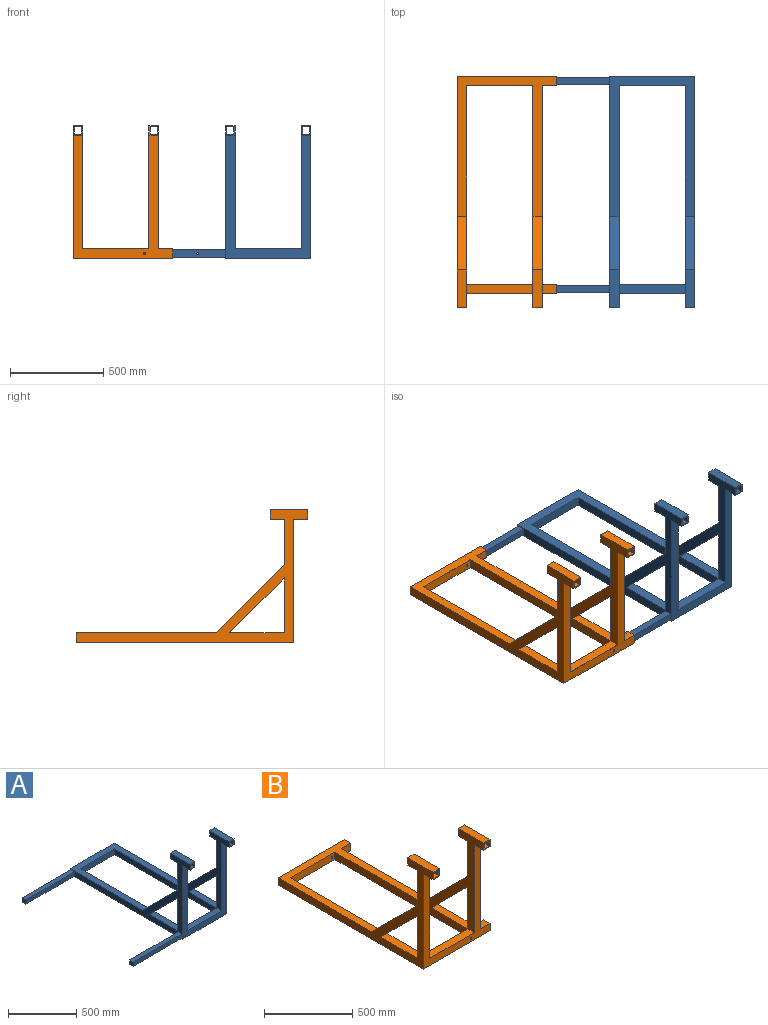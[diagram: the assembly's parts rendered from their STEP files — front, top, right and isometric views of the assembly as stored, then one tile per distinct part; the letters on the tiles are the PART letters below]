
ASSEMBLY  parts=2 mates=1
PART A: 53 faces, bbox 965.2x1244.6x711.2 mm
  f0: plane 50.8x50.8mm, normal (0,1,0), area 1129mm2, adj f9,f12,f13,f24,f35,f36,f37,f38
  f1: plane 50.8x50.8mm, normal (0,-1,0), area 1129mm2, adj f9,f12,f13,f30,f35,f36,f37,f38
  f2: plane 50.8x50.8mm, normal (0,1,0), area 1129mm2, adj f11,f15,f16,f17,f31,f32,f33,f34
  f3: plane 50.8x50.8mm, normal (0,-1,0), area 1129mm2, adj f11,f15,f16,f29,f31,f32,f33,f34
  f4: plane 660.4x457.2mm, normal (0,-1,0), area 85161.1mm2, adj f5,f9,f11,f13,f14,f15,f29,f30
  f5: plane 1168.4x457.2mm, normal (0,0,-1), area 154838.4mm2, adj f4,f9,f10,f11,f13,f15,f27,f28
  f6: plane 751.48x457.2mm, normal (0,0,1), area 94414.8mm2, adj f9,f10,f11,f13,f15,f19,f22,f27
  f7: plane 294.28x50.8mm, normal (0,0,1), area 14949.4mm2, adj f11,f15,f20,f21
  f8: plane 294.28x50.8mm, normal (0,0,1), area 14949.4mm2, adj f9,f13,f25,f26
  f9: plane 1244.6x711.2mm, normal (1,0,0), area 124367mm2, adj f0,f1,f4,f5,f6,f8,f10,f12
  f10: plane 457.2x50.8mm, normal (0,1,0), area 23225.8mm2, adj f5,f6,f9,f11
  f11: plane 1244.6x711.2mm, normal (-1,0,0), area 121463.8mm2, adj f2,f3,f4,f5,f6,f7,f10,f16
  f12: plane 203.2x50.8mm, normal (0,0,1), area 10322.6mm2, adj f0,f1,f9,f13
  f13: plane 1193.8x711.2mm, normal (-1,0,0), area 119205.7mm2, adj f0,f1,f4,f5,f6,f8,f12,f14
  f14: plane 355.6x50.8mm, normal (0,0,1), area 18064.5mm2, adj f4,f13,f15,f28
  f15: plane 1193.8x711.2mm, normal (1,0,0), area 119205.7mm2, adj f2,f3,f4,f5,f6,f7,f14,f16
  f16: plane 203.2x50.8mm, normal (0,0,1), area 10322.6mm2, adj f2,f3,f11,f15
  f17: plane 76.2x50.8mm, normal (0,0,-1), area 3871mm2, adj f2,f11,f15,f18
  f18: plane 243.48x50.8mm, normal (0,1,0), area 12368.7mm2, adj f11,f15,f17,f19
  f19: plane 366.12x366.12mm, normal (0,0.71,0.71), area 26302.9mm2, adj f6,f11,f15,f18
  f20: plane 294.28x294.28mm, normal (0,-0.71,-0.71), area 21141.6mm2, adj f7,f11,f15,f21
  f21: plane 294.28x50.8mm, normal (0,1,0), area 14949.4mm2, adj f7,f11,f15,f20
  f22: plane 366.12x366.12mm, normal (0,0.71,0.71), area 26302.9mm2, adj f6,f9,f13,f23
  f23: plane 243.48x50.8mm, normal (0,1,0), area 12368.7mm2, adj f9,f13,f22,f24
  f24: plane 76.2x50.8mm, normal (0,0,-1), area 3871mm2, adj f0,f9,f13,f23
  f25: plane 294.28x50.8mm, normal (0,1,0), area 14949.4mm2, adj f8,f9,f13,f26
  f26: plane 294.28x294.28mm, normal (0,-0.71,-0.71), area 21141.6mm2, adj f8,f9,f13,f25
  f27: plane 355.6x50.8mm, normal (0,-1,0), area 18064.5mm2, adj f5,f6,f13,f15
  f28: plane 355.6x50.8mm, normal (0,1,0), area 18064.5mm2, adj f5,f13,f14,f15
  f29: plane 76.2x50.8mm, normal (0,0,-1), area 3871mm2, adj f3,f4,f11,f15
  f30: plane 76.2x50.8mm, normal (0,0,-1), area 3871mm2, adj f1,f4,f9,f13
  f31: plane 203.2x38.1mm, normal (-1,0,0), area 7741.9mm2, adj f2,f3,f32,f34
  f32: plane 203.2x38.1mm, normal (0,0,-1), area 7741.9mm2, adj f2,f3,f31,f33
  f33: plane 203.2x38.1mm, normal (1,0,0), area 7741.9mm2, adj f2,f3,f32,f34
  f34: plane 203.2x38.1mm, normal (0,0,1), area 7741.9mm2, adj f2,f3,f31,f33
  f35: plane 203.2x38.1mm, normal (-1,0,0), area 7741.9mm2, adj f0,f1,f36,f38
  f36: plane 203.2x38.1mm, normal (0,0,-1), area 7741.9mm2, adj f0,f1,f35,f37
  f37: plane 203.2x38.1mm, normal (1,0,0), area 7741.9mm2, adj f0,f1,f36,f38
  f38: plane 203.2x38.1mm, normal (0,0,1), area 7741.9mm2, adj f0,f1,f35,f37
  f39: plane 508x38.1mm, normal (0,-1,0), area 19101.4mm2, adj f11,f40,f42,f43,f51,f52
  f40: plane 508x38.1mm, normal (0,0,1), area 19354.8mm2, adj f11,f39,f41,f43
  f41: plane 508x38.1mm, normal (0,1,0), area 19101.4mm2, adj f11,f40,f42,f43,f51,f52
  f42: plane 508x38.1mm, normal (0,0,-1), area 19354.8mm2, adj f11,f39,f41,f43
  f43: plane 38.1x38.1mm, normal (-1,0,0), area 1451.6mm2, adj f39,f40,f41,f42
  f44: plane 508x38.1mm, normal (0,0,1), area 19354.8mm2, adj f11,f45,f47,f48
  f45: plane 508x38.1mm, normal (0,1,0), area 19101.4mm2, adj f11,f44,f46,f48,f49,f50
  f46: plane 508x38.1mm, normal (0,0,-1), area 19354.8mm2, adj f11,f45,f47,f48
  f47: plane 508x38.1mm, normal (0,-1,0), area 19101.4mm2, adj f11,f44,f46,f48,f49,f50
  f48: plane 38.1x38.1mm, normal (-1,0,0), area 1451.6mm2, adj f44,f45,f46,f47
  f49: cylinder r=6.35mm len=38.1mm, axis (0,-1,0), area 1520.1mm2, adj f45,f47
  f50: cylinder r=6.35mm len=38.1mm, axis (0,-1,0), area 1520.1mm2, adj f45,f47
  f51: cylinder r=6.35mm len=38.1mm, axis (0,-1,0), area 1520.1mm2, adj f39,f41
  f52: cylinder r=6.35mm len=38.1mm, axis (0,-1,0), area 1520.1mm2, adj f39,f41
PART B: 74 faces, bbox 533.4x1244.6x711.2 mm
  f0: plane 50.8x50.8mm, normal (1,0,0), area 1129mm2, adj f7,f10,f12,f31,f47,f50,f52,f67
  f1: plane 50.8x50.8mm, normal (0,1,0), area 1129mm2, adj f13,f14,f15,f27,f40,f41,f42,f43
  f2: plane 50.8x50.8mm, normal (0,-1,0), area 1129mm2, adj f13,f14,f15,f35,f40,f41,f42,f43
  f3: plane 50.8x50.8mm, normal (0,1,0), area 1129mm2, adj f16,f17,f18,f20,f36,f37,f38,f39
  f4: plane 50.8x50.8mm, normal (0,-1,0), area 1129mm2, adj f16,f17,f18,f34,f36,f37,f38,f39
  f5: plane 660.4x533.4mm, normal (0,-1,0), area 88905.4mm2, adj f6,f7,f9,f11,f13,f15,f16,f18
  f6: plane 50.8x50.8mm, normal (1,0,0), area 1129mm2, adj f5,f7,f11,f30,f45,f47,f51,f66
  f7: plane 1168.4x533.4mm, normal (0,0,-1), area 162580.3mm2, adj f0,f5,f6,f12,f13,f15,f16,f18
  f8: plane 294.28x50.8mm, normal (0,0,1), area 14949.4mm2, adj f13,f15,f28,f29
  f9: plane 355.6x50.8mm, normal (0,0,1), area 18064.5mm2, adj f5,f15,f16,f32
  f10: plane 751.48x533.4mm, normal (0,0,1), area 98285.7mm2, adj f0,f12,f13,f15,f16,f18,f22,f25
  f11: plane 76.2x50.8mm, normal (0,0,1), area 3871mm2, adj f5,f6,f13,f30
  f12: plane 533.4x50.8mm, normal (0,1,0), area 26970mm2, adj f0,f7,f10,f18,f72
  f13: plane 1193.8x711.2mm, normal (1,0,0), area 119205.7mm2, adj f1,f2,f5,f7,f8,f10,f11,f14
  f14: plane 203.2x50.8mm, normal (0,0,1), area 10322.6mm2, adj f1,f2,f13,f15
  f15: plane 1193.8x711.2mm, normal (-1,0,0), area 119205.7mm2, adj f1,f2,f5,f7,f8,f9,f10,f14
  f16: plane 1193.8x711.2mm, normal (1,0,0), area 119205.7mm2, adj f3,f4,f5,f7,f9,f10,f17,f19
  f17: plane 203.2x50.8mm, normal (0,0,1), area 10322.6mm2, adj f3,f4,f16,f18
  f18: plane 1244.6x711.2mm, normal (-1,0,0), area 124367mm2, adj f3,f4,f5,f7,f10,f12,f17,f19
  f19: plane 294.28x50.8mm, normal (0,0,1), area 14949.4mm2, adj f16,f18,f23,f24
  f20: plane 76.2x50.8mm, normal (0,0,-1), area 3871mm2, adj f3,f16,f18,f21
  f21: plane 243.48x50.8mm, normal (0,1,0), area 12368.7mm2, adj f16,f18,f20,f22
  f22: plane 366.12x366.12mm, normal (0,0.71,0.71), area 26302.9mm2, adj f10,f16,f18,f21
  f23: plane 294.28x294.28mm, normal (0,-0.71,-0.71), area 21141.6mm2, adj f16,f18,f19,f24
  f24: plane 294.28x50.8mm, normal (0,1,0), area 14949.4mm2, adj f16,f18,f19,f23
  f25: plane 366.12x366.12mm, normal (0,0.71,0.71), area 26302.9mm2, adj f10,f13,f15,f26
  f26: plane 243.48x50.8mm, normal (0,1,0), area 12368.7mm2, adj f13,f15,f25,f27
  f27: plane 76.2x50.8mm, normal (0,0,-1), area 3871mm2, adj f1,f13,f15,f26
  f28: plane 294.28x50.8mm, normal (0,1,0), area 14949.4mm2, adj f8,f13,f15,f29
  f29: plane 294.28x294.28mm, normal (0,-0.71,-0.71), area 21141.6mm2, adj f8,f13,f15,f28
  f30: plane 76.2x50.8mm, normal (0,1,0), area 3871mm2, adj f6,f7,f11,f13
  f31: plane 76.2x50.8mm, normal (0,-1,0), area 3871mm2, adj f0,f7,f10,f13
  f32: plane 355.6x50.8mm, normal (0,1,0), area 17937.8mm2, adj f7,f9,f15,f16,f71
  f33: plane 355.6x50.8mm, normal (0,-1,0), area 17937.8mm2, adj f7,f10,f15,f16,f70
  f34: plane 76.2x50.8mm, normal (0,0,-1), area 3871mm2, adj f4,f5,f16,f18
  f35: plane 76.2x50.8mm, normal (0,0,-1), area 3871mm2, adj f2,f5,f13,f15
  f36: plane 203.2x38.1mm, normal (-1,0,0), area 7741.9mm2, adj f3,f4,f37,f39
  f37: plane 203.2x38.1mm, normal (0,0,-1), area 7741.9mm2, adj f3,f4,f36,f38
  f38: plane 203.2x38.1mm, normal (1,0,0), area 7741.9mm2, adj f3,f4,f37,f39
  f39: plane 203.2x38.1mm, normal (0,0,1), area 7741.9mm2, adj f3,f4,f36,f38
  f40: plane 203.2x38.1mm, normal (-1,0,0), area 7741.9mm2, adj f1,f2,f41,f43
  f41: plane 203.2x38.1mm, normal (0,0,-1), area 7741.9mm2, adj f1,f2,f40,f42
  f42: plane 203.2x38.1mm, normal (1,0,0), area 7741.9mm2, adj f1,f2,f41,f43
  f43: plane 203.2x38.1mm, normal (0,0,1), area 7741.9mm2, adj f1,f2,f40,f42
  f44: plane 38.1x38.1mm, normal (0,0,-1), area 1451.6mm2, adj f45,f55,f56,f58
  f45: plane 654.05x527.05mm, normal (0,1,0), area 66889.3mm2, adj f6,f44,f46,f47,f49,f51,f53,f54
  f46: plane 38.1x38.1mm, normal (0,0,-1), area 1451.6mm2, adj f45,f53,f54,f63
  f47: plane 1155.7x527.05mm, normal (0,0,1), area 122419.1mm2, adj f0,f6,f45,f52,f53,f54,f55,f56
  f48: plane 315.96x38.1mm, normal (0,0,-1), area 12038.1mm2, adj f53,f54,f64,f65
  f49: plane 368.3x38.1mm, normal (0,0,-1), area 14032.2mm2, adj f45,f54,f55,f68
  f50: plane 747.76x527.05mm, normal (0,0,-1), area 74156.7mm2, adj f0,f52,f53,f54,f55,f56,f59,f62
  f51: plane 82.55x38.1mm, normal (0,0,-1), area 3145.2mm2, adj f6,f45,f53,f66
  f52: plane 527.05x38.1mm, normal (0,-1,0), area 19953.9mm2, adj f0,f47,f50,f56,f72
  f53: plane 1117.6x654.05mm, normal (-1,0,0), area 83072.4mm2, adj f45,f46,f47,f48,f50,f51,f62,f63
  f54: plane 1117.6x654.05mm, normal (1,0,0), area 83072.4mm2, adj f45,f46,f47,f48,f49,f50,f62,f63
  f55: plane 1117.6x654.05mm, normal (-1,0,0), area 83072.4mm2, adj f44,f45,f47,f49,f50,f57,f58,f59
  f56: plane 1155.7x654.05mm, normal (1,0,0), area 85975.6mm2, adj f44,f45,f47,f50,f52,f57,f58,f59
  f57: plane 315.96x38.1mm, normal (0,0,-1), area 12038.1mm2, adj f55,f56,f60,f61
  f58: plane 246.11x38.1mm, normal (0,-1,0), area 9376.8mm2, adj f44,f55,f56,f59
  f59: plane 369.84x369.84mm, normal (0,-0.71,-0.71), area 19927.6mm2, adj f50,f55,f56,f58
  f60: plane 315.96x315.96mm, normal (0,0.71,0.71), area 17024.4mm2, adj f55,f56,f57,f61
  f61: plane 315.96x38.1mm, normal (0,-1,0), area 12038.1mm2, adj f55,f56,f57,f60
  f62: plane 369.84x369.84mm, normal (0,-0.71,-0.71), area 19927.6mm2, adj f50,f53,f54,f63
  f63: plane 246.11x38.1mm, normal (0,-1,0), area 9376.8mm2, adj f46,f53,f54,f62
  f64: plane 315.96x38.1mm, normal (0,-1,0), area 12038.1mm2, adj f48,f53,f54,f65
  f65: plane 315.96x315.96mm, normal (0,0.71,0.71), area 17024.4mm2, adj f48,f53,f54,f64
  f66: plane 82.55x38.1mm, normal (0,-1,0), area 3145.2mm2, adj f6,f47,f51,f53
  f67: plane 82.55x38.1mm, normal (0,1,0), area 3145.2mm2, adj f0,f47,f50,f53
  f68: plane 368.3x38.1mm, normal (0,-1,0), area 13905.6mm2, adj f47,f49,f54,f55,f71
  f69: plane 368.3x38.1mm, normal (0,1,0), area 13905.6mm2, adj f47,f50,f54,f55,f70
  f70: cylinder r=6.35mm len=12.7mm, axis (0,-1,0), area 253.4mm2, adj f33,f69
  f71: cylinder r=6.35mm len=12.7mm, axis (0,-1,0), area 253.4mm2, adj f32,f68
  f72: cylinder r=6.35mm len=12.7mm, axis (0,-1,0), area 253.4mm2, adj f12,f52
  f73: cylinder r=6.35mm len=12.7mm, axis (0,-1,0), area 253.4mm2, adj f5,f45
PLACE A t=(5.09,0,0)mm
PLACE B at identity fixed
MATE slider B.f6 <-> A.f43  axis (-1,0,0) through (-101.6,6.35,6.35)mm
